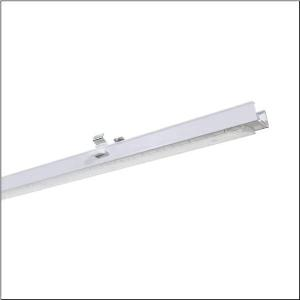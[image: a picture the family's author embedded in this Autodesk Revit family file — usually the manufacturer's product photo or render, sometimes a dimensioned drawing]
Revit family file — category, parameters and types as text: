
# Revit family: trunking_flex_31_51re12ma16b
name_source: partatom
category: Lighting Fixtures
units: mm (PartAtom-declared; Revit-internal decimal feet)

## family parameters
Cut with Voids When Loaded = No
Host = Face
Light Source = No
Part Type = Normal
Room Calculation Point = No
Round Connector Dimension = Use Diameter
Shared = No

## types (1)
- --- (1 x LED, 6400 lm, 40 W, 3500K)
    Apparent Load = 40 VA
    CIE Flux Codes = 65 91 98 99 100
    Color Rendering = 80
    Color Temperature = 3500K
    Default Elevation = 1800 mm
    Description = Trunking Flex 31, luminaire insert, of extruded aluminium section, coated, traffic white (RAL 9016), length: 1.172mm, width: 91mm, height: 53mm, LED rated luminous flux: 6.400lm, light colour: 835, control gear: ON/OFF Multilumen, with system connector: socket, mains connection: 220..240V, AC, 50/60Hz, rated input power: 40W, luminous flux adjustable on luminaire in four steps (3420/4540/5580/6630lm), connected load according to luminous flux setting (20/26/33/40W), primary light control with lens, of plastic, primary optical cover: cover, of PMMA, light emission: direct distribution, protection rating (complete): IP20, insulation class (complete): insulation class I (protective earthing), certification: CE, UKCA, impact resistance: IK02, permissible ambient temperature for indoor applications: -20..+40°C, packaging unit: 1 piece
    Height = 58 mm
    Lamp = 1 x LED
    Lamp Light Flux = 6400 lm
    Lamp Power = 40 W
    Lamp count = 1
    Length = 1172 mm
    Luminous efficacy = 160 lm/W
    Manufacturer = Siteco
    ModVariant = No
    Model = 51RE12MA16B
    Mounting Place = Ceiling
    Mounting Type = Pendant
    Number of Poles = 1
    OnlyDefault = Yes
    Power Factor = 1
    Product Name = Trunking Flex 31
    Product group = luminaire insert
    ProductGroupID = 901
    Protection Class = Protection class I
    Protection Degree = IP 20
    RLX_Detail_Level = 1
    RLX_Emergency_Light_Flux = 0 lm
    RLX_Emergency_Type = 0
    RLX_Emergency_Type_DB = No
    RlxData = <blob elided: 19993 chars, md5=e1b3b688>
    Socket = socket
    Standby Power = 0 W
    System Light Flux = 6400 lm
    System Power = 40 W
    Type Comments = factory setting: luminous flux: 100 % | (ON | ON) | 300 mA
    Type Image = l_1266702.jpg
    URL = http://relux.com
    VarID = @adj_018689
    Voltage = 0 V
    Weight = 0.00 kg
    Width = 65 mm

## geometry (parser evidence)
native form markers: Blend x4, Sweep x10
no freeform markers — native parametric forms only
